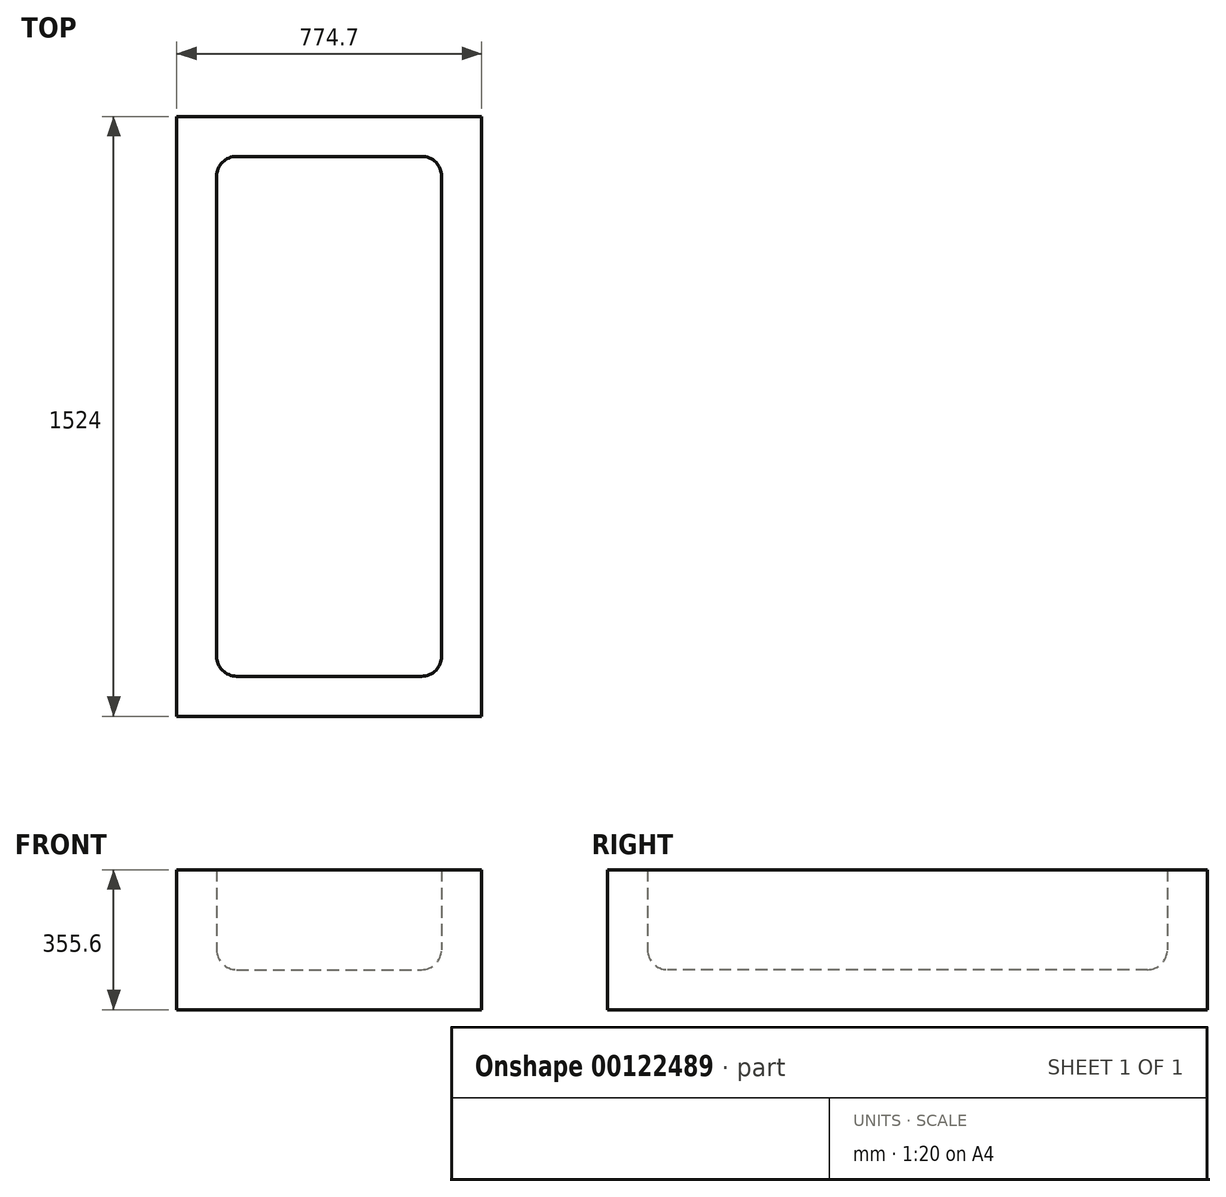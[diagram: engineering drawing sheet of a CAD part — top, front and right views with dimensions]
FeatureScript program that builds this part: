
annotation { "Feature Type Name" : "Feature", "Feature Type Description" : "" }
export const myFeature = defineFeature(function(context is Context, id is Id, definition is map)
    precondition{}
    {
        {
            var Q0;
            Q0=qCreatedBy(makeId("Top.planeOp"),FACE);
            var sketch = newSketch(context, id + "F0", { "sketchPlane" : qUnion([Q0])});
            skLineSegment(sketch, "E0.bottom", {"start": v(-1082.05, 748.68) * mm, "end": v(-307.35, 748.68) * mm});
            skLineSegment(sketch, "E0.top", {"start": v(-1082.05, -775.32) * mm, "end": v(-307.35, -775.32) * mm});
            skLineSegment(sketch, "E0.left", {"start": v(-1082.05, 748.68) * mm, "end": v(-1082.05, -775.32) * mm});
            skLineSegment(sketch, "E0.right", {"start": v(-307.35, 748.68) * mm, "end": v(-307.35, -775.32) * mm});
            skSolve(sketch);
        }
        {
            var Q0;
            Q0 = qSketchRegion(id + "F0", true);
            extrude(context, id + "F1", {"entities" : qUnion([Q0]), "depth" : 355.6 * mm});
        }
        {
            var Q0;
            Q0=makeQuery(id+"F1.opExtrude","CAP_FACE",FACE,{"disambiguationData":[OSD([sQuery(id+"F0.wireOp",EDGE,"E0.bottom"),sQuery(id+"F0.wireOp",EDGE,"E0.top"),sQuery(id+"F0.wireOp",EDGE,"E0.left"),sQuery(id+"F0.wireOp",EDGE,"E0.right")])],"isStart":false});
            shell(context, id + "F2", {"entities" : qUnion([Q0]), "thickness" : 101.6 * mm});
        }
        {
            var Q0;
            Q0=makeQuery(id+"F2.opShell","OFFSET_FACE",FACE,{"disambiguationData":[OSD([sQuery(id+"F0.wireOp",EDGE,"E0.bottom"),sQuery(id+"F0.wireOp",EDGE,"E0.top"),sQuery(id+"F0.wireOp",EDGE,"E0.left"),sQuery(id+"F0.wireOp",EDGE,"E0.right")])]});
            var Q1;
            Q1=makeQuery(id+"F2.opShell","OFFSET_EDGE",EDGE,{"disambiguationData":[OSD([sQuery(id+"F0.wireOp",EDGE,"E0.top"),sQuery(id+"F0.wireOp",EDGE,"E0.right")])]});
            var Q2;
            Q2=makeQuery(id+"F2.opShell","OFFSET_EDGE",EDGE,{"disambiguationData":[OSD([sQuery(id+"F0.wireOp",EDGE,"E0.bottom"),sQuery(id+"F0.wireOp",EDGE,"E0.right")])]});
            var Q3;
            Q3=makeQuery(id+"F2.opShell","OFFSET_EDGE",EDGE,{"disambiguationData":[OSD([sQuery(id+"F0.wireOp",EDGE,"E0.bottom"),sQuery(id+"F0.wireOp",EDGE,"E0.left")])]});
            var Q4;
            Q4=makeQuery(id+"F2.opShell","OFFSET_EDGE",EDGE,{"disambiguationData":[OSD([sQuery(id+"F0.wireOp",EDGE,"E0.top"),sQuery(id+"F0.wireOp",EDGE,"E0.left")])]});
            fillet(context, id + "F3", {"entities" : qUnion([Q0, Q1, Q2, Q3, Q4]), "radius" : 50.8 * mm, "tangentPropagation" : true, "allowEdgeOverflow" : false});
        }
    });
